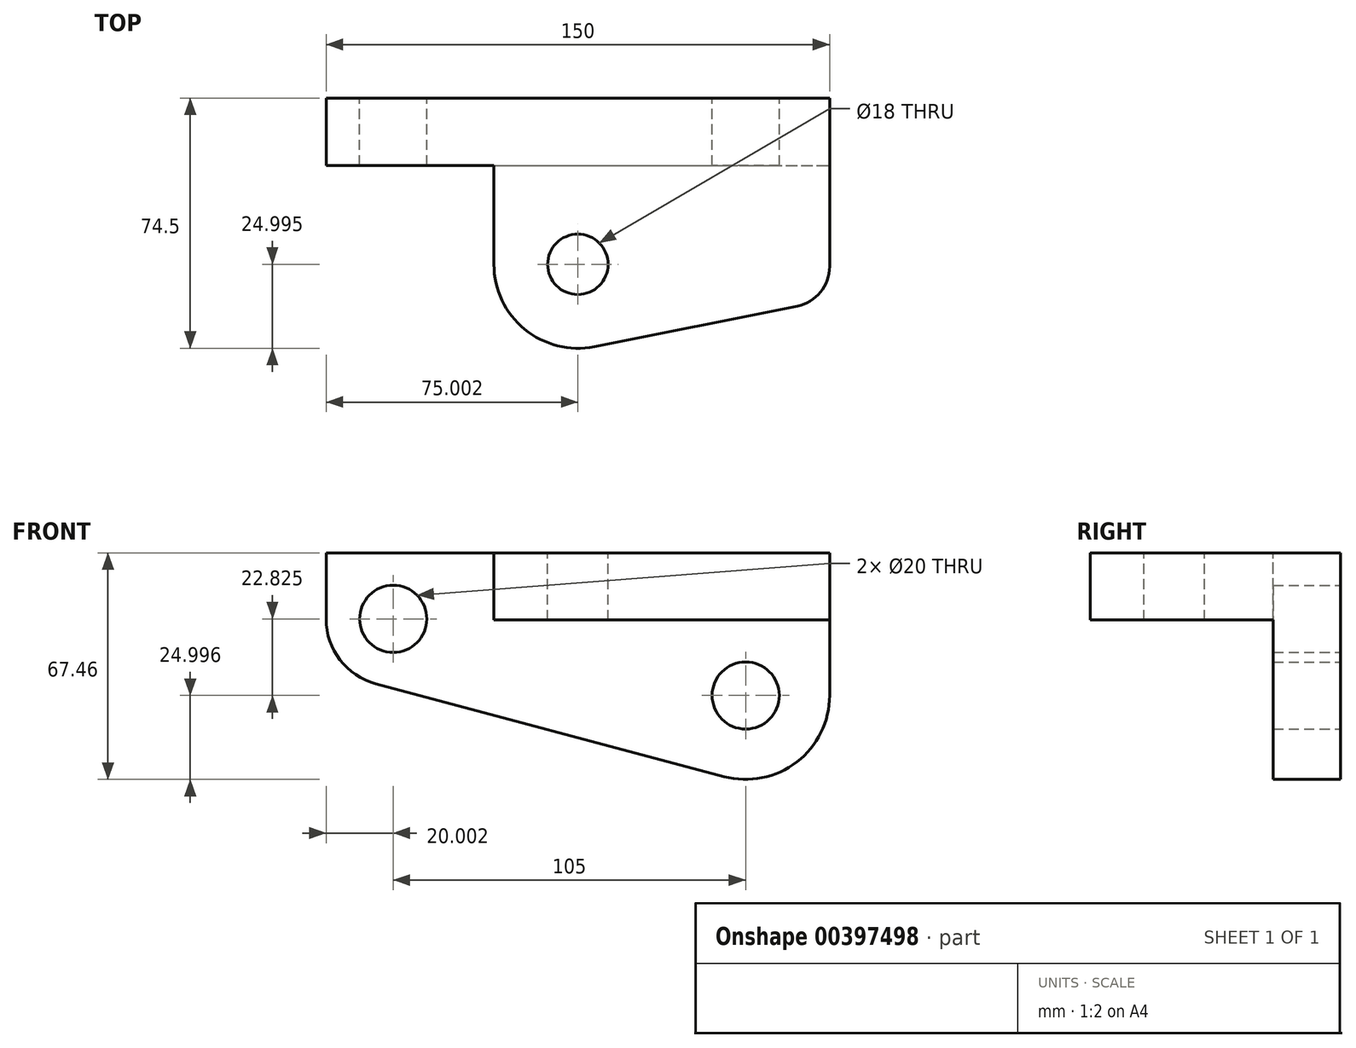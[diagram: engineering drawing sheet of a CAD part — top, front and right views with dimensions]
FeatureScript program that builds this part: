
annotation { "Feature Type Name" : "Feature", "Feature Type Description" : "" }
export const myFeature = defineFeature(function(context is Context, id is Id, definition is map)
    precondition{}
    {
        {
            var Q0;
            Q0=qCreatedBy(makeId("Front.planeOp"),FACE);
            var sketch = newSketch(context, id + "F0", { "sketchPlane" : qUnion([Q0])});
            skLineSegment(sketch, "E0", {"start": v(-76.38, 0.5) * mm, "end": v(-76.38, 20.14) * mm});
            skLineSegment(sketch, "E1", {"start": v(-76.38, 20.14) * mm, "end": v(73.62, 20.14) * mm});
            skLineSegment(sketch, "E2", {"start": v(73.62, 20.14) * mm, "end": v(73.62, -22.32) * mm});
            skLineSegment(sketch, "E3", {"start": v(-61.53, -18.82) * mm, "end": v(42.18, -46.48) * mm});
            skPoint(sketch, "E4.visualSharp", {"position": v(-76.38, -14.86) * mm});
            skArc(sketch, "E4.filletArc", {"start": v(-76.38, 0.5) * mm, "mid": v(-72.24, -11.68) * mm, "end": v(-61.53, -18.82) * mm});
            skPoint(sketch, "E5.visualSharp", {"position": v(73.62, -54.86) * mm});
            skArc(sketch, "E5.filletArc", {"start": v(42.18, -46.48) * mm, "mid": v(63.85, -42.15) * mm, "end": v(73.62, -22.32) * mm});
            skCircle(sketch, "E6", {"center": v(-56.38, 0.5) * mm, "radius": 10 * mm});
            skCircle(sketch, "E7", {"center": v(48.62, -22.32) * mm, "radius": 10 * mm});
            skSolve(sketch);
        }
        {
            var Q0;
            Q0=makeQuery(id+"F0.imprint","IMPRINT",FACE,{"disambiguationData":[TD([[makeQuery(id+"F0.imprint","IMPRINT",EDGE,{"derivedFrom":sQuery(id+"F0.wireOp",EDGE,"E0")}),-1.0]])]});
            extrude(context, id + "F1", {"entities" : qUnion([Q0]), "depth" : 20 * mm});
        }
        {
            var Q0;
            Q0=makeQuery(id+"F1.opExtrude","SWEPT_FACE",FACE,{"disambiguationData":[OSD([sQuery(id+"F0.wireOp",EDGE,"E1")])]});
            var sketch = newSketch(context, id + "F2", { "sketchPlane" : qUnion([Q0])});
            skLineSegment(sketch, "E8", {"start": v(73.62, 0) * mm, "end": v(73.62, -60) * mm});
            skLineSegment(sketch, "E9", {"start": v(73.62, 0) * mm, "end": v(-26.38, 0) * mm});
            skLineSegment(sketch, "E10", {"start": v(-26.38, 0) * mm, "end": v(-26.38, -49.5) * mm});
            skLineSegment(sketch, "E11", {"start": v(3.52, -74.02) * mm, "end": v(73.62, -60) * mm});
            skPoint(sketch, "E12.visualSharp", {"position": v(-26.38, -80) * mm});
            skArc(sketch, "E12.filletArc", {"start": v(-26.38, -49.5) * mm, "mid": v(-17.23, -68.84) * mm, "end": v(3.52, -74.02) * mm});
            skCircle(sketch, "E13", {"center": v(-1.38, -49.5) * mm, "radius": 9 * mm});
            skSolve(sketch);
        }
        {
            var Q0;
            {var subQ4=sQuery(id+"F2.wireOp",EDGE,"E11");Q0=makeQuery(id+"F2.imprint","IMPRINT",FACE,{"disambiguationData":[TD([[makeQuery(id+"F2.imprint","IMPRINT",EDGE,{"derivedFrom":subQ4}),1.0]])]});}
            extrude(context, id + "F3", {"entities" : qUnion([Q0]), "operationType" : NewBodyOperationType.ADD, "oppositeDirection" : true, "depth" : 20 * mm});
        }
        {
            var Q0;
            Q0=makeQuery(id+"F3.opExtrude","SWEPT_EDGE",EDGE,{"disambiguationData":[OSD([sQuery(id+"F2.wireOp",EDGE,"E8"),sQuery(id+"F2.wireOp",EDGE,"E11")])]});
            fillet(context, id + "F4", {"entities" : qUnion([Q0]), "radius" : 12 * mm, "tangentPropagation" : true, "allowEdgeOverflow" : false});
        }
    });
